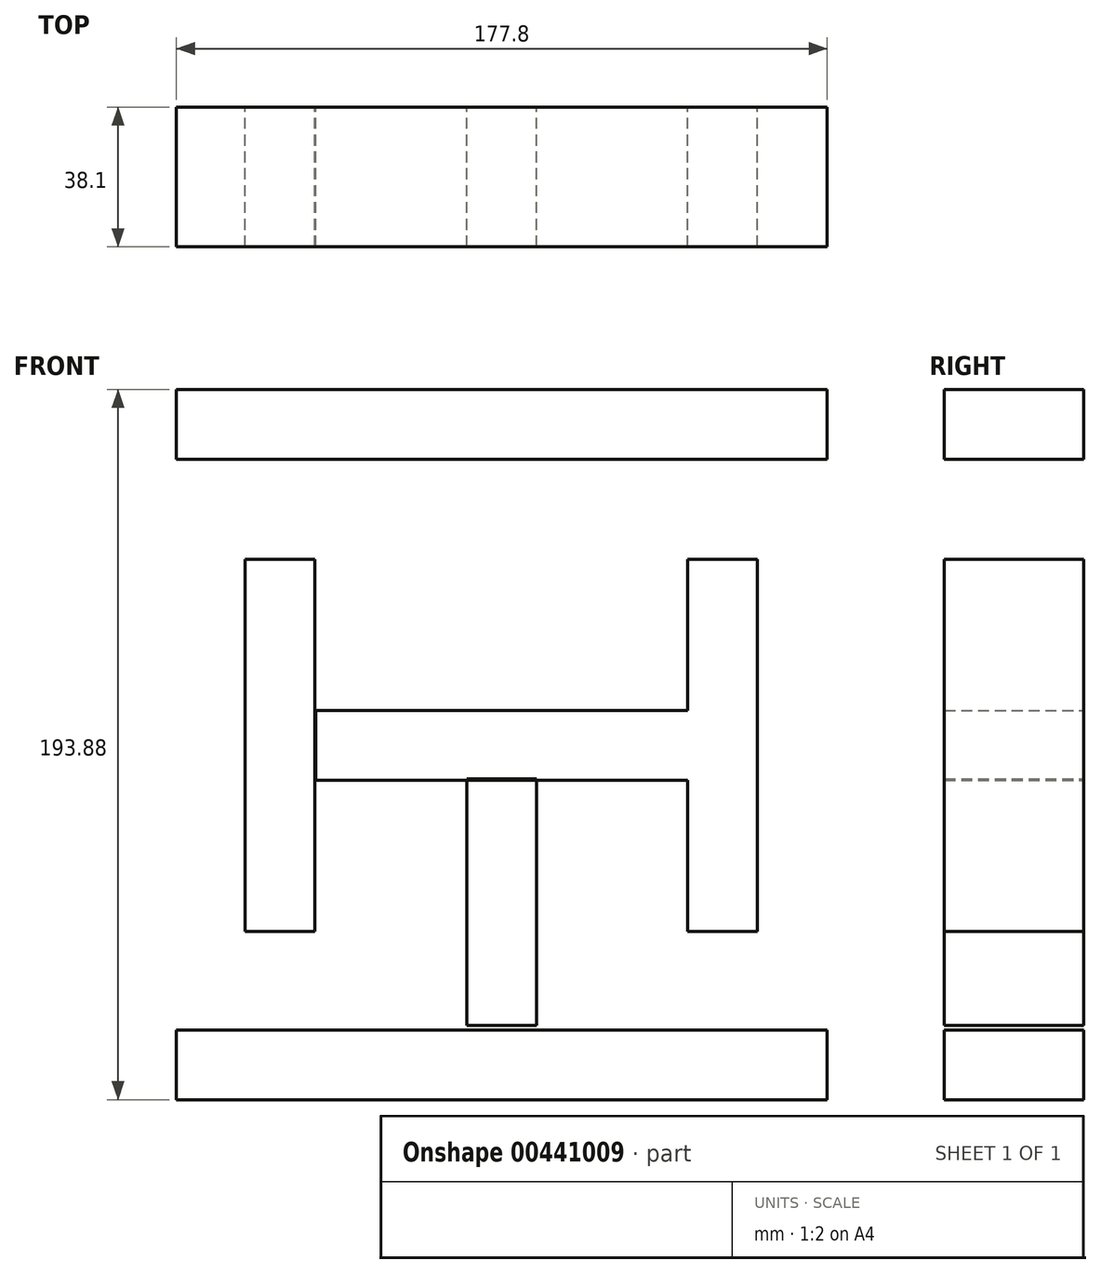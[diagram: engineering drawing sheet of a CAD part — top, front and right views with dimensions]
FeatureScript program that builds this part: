
annotation { "Feature Type Name" : "Feature", "Feature Type Description" : "" }
export const myFeature = defineFeature(function(context is Context, id is Id, definition is map)
    precondition{}
    {
        {
            var Q0;
            Q0=qCreatedBy(makeId("Front.planeOp"),FACE);
            var sketch = newSketch(context, id + "F0", { "sketchPlane" : qUnion([Q0])});
            skLineSegment(sketch, "E0.bottom", {"start": v(-88.9, 97.2) * mm, "end": v(88.9, 97.2) * mm});
            skLineSegment(sketch, "E0.top", {"start": v(-88.9, 78.15) * mm, "end": v(88.9, 78.15) * mm});
            skLineSegment(sketch, "E0.left", {"start": v(-88.9, 97.2) * mm, "end": v(-88.9, 78.15) * mm});
            skLineSegment(sketch, "E0.right", {"start": v(88.9, 97.2) * mm, "end": v(88.9, 78.15) * mm});
            skPoint(sketch, "E0.middle", {"position": v(0, 87.68) * mm});
            skLineSegment(sketch, "E1.bottom", {"start": v(-88.9, -96.68) * mm, "end": v(88.9, -96.68) * mm});
            skLineSegment(sketch, "E1.top", {"start": v(-88.9, -77.63) * mm, "end": v(88.9, -77.63) * mm});
            skLineSegment(sketch, "E1.left", {"start": v(-88.9, -96.68) * mm, "end": v(-88.9, -77.63) * mm});
            skLineSegment(sketch, "E1.right", {"start": v(88.9, -96.68) * mm, "end": v(88.9, -77.63) * mm});
            skPoint(sketch, "E1.middle", {"position": v(0, -87.16) * mm});
            skLineSegment(sketch, "E2.bottom", {"start": v(-9.53, 78.15) * mm, "end": v(9.52, 78.15) * mm});
            skLineSegment(sketch, "E2.top", {"start": v(-9.52, 10.84) * mm, "end": v(9.53, 10.84) * mm});
            skLineSegment(sketch, "E2.left", {"start": v(-9.53, 78.15) * mm, "end": v(-9.52, 10.84) * mm});
            skLineSegment(sketch, "E2.right", {"start": v(9.52, 78.15) * mm, "end": v(9.53, 10.84) * mm});
            skPoint(sketch, "E2.middle", {"position": v(0, 44.5) * mm});
            skLineSegment(sketch, "E3.bottom", {"start": v(-9.53, -9.12) * mm, "end": v(9.53, -9.12) * mm});
            skLineSegment(sketch, "E3.top", {"start": v(-9.53, -76.43) * mm, "end": v(9.52, -76.43) * mm});
            skLineSegment(sketch, "E3.left", {"start": v(-9.53, -9.12) * mm, "end": v(-9.53, -76.43) * mm});
            skLineSegment(sketch, "E3.right", {"start": v(9.53, -9.12) * mm, "end": v(9.52, -76.43) * mm});
            skPoint(sketch, "E3.middle", {"position": v(0, -42.78) * mm});
            skLineSegment(sketch, "E4.bottom", {"start": v(-50.8, 9.53) * mm, "end": v(50.8, 9.53) * mm});
            skLineSegment(sketch, "E4.top", {"start": v(-50.8, -9.52) * mm, "end": v(50.8, -9.52) * mm});
            skLineSegment(sketch, "E4.left", {"start": v(-50.8, 9.53) * mm, "end": v(-50.8, -9.52) * mm});
            skLineSegment(sketch, "E4.right", {"start": v(50.8, 9.53) * mm, "end": v(50.8, -9.52) * mm});
            skPoint(sketch, "E4.middle", {"position": v(0, 0) * mm});
            skLineSegment(sketch, "E5.bottom", {"start": v(50.8, 50.8) * mm, "end": v(69.85, 50.8) * mm});
            skLineSegment(sketch, "E5.top", {"start": v(50.8, -50.8) * mm, "end": v(69.85, -50.8) * mm});
            skLineSegment(sketch, "E5.left", {"start": v(50.8, 50.8) * mm, "end": v(50.8, -50.8) * mm});
            skLineSegment(sketch, "E5.right", {"start": v(69.85, 50.8) * mm, "end": v(69.85, -50.8) * mm});
            skPoint(sketch, "E5.middle", {"position": v(60.33, 0) * mm});
            skPoint(sketch, "E5.middle.positionSnap0", {"position": v(50.8, 0) * mm});
            skPoint(sketch, "E5.cornerSnap0", {"position": v(50.8, 0) * mm});
            skPoint(sketch, "E5.centerSnap0", {"position": v(50.8, 0) * mm});
            skLineSegment(sketch, "E6.bottom", {"start": v(-70.2, 50.8) * mm, "end": v(-51.15, 50.8) * mm});
            skLineSegment(sketch, "E6.top", {"start": v(-70.2, -50.8) * mm, "end": v(-51.15, -50.8) * mm});
            skLineSegment(sketch, "E6.left", {"start": v(-70.2, 50.8) * mm, "end": v(-70.2, -50.8) * mm});
            skLineSegment(sketch, "E6.right", {"start": v(-51.15, 50.8) * mm, "end": v(-51.15, -50.8) * mm});
            skPoint(sketch, "E6.middle", {"position": v(-60.67, 0) * mm});
            skPoint(sketch, "E6.middle.positionSnap0", {"position": v(-50.8, 0) * mm});
            skPoint(sketch, "E6.centerSnap0", {"position": v(-50.8, 0) * mm});
            skSolve(sketch);
        }
        {
            var Q0;
            Q0=makeQuery(id+"F0.imprint","IMPRINT",FACE,{"disambiguationData":[TD([[makeQuery(id+"F0.imprint","IMPRINT",EDGE,{"derivedFrom":sQuery(id+"F0.wireOp",EDGE,"E6.bottom")}),-1.0]])]});
            var Q1;
            {var subQ3=sQuery(id+"F0.wireOp",EDGE,"E5.bottom");Q1=makeQuery(id+"F0.imprint","IMPRINT",FACE,{"disambiguationData":[TD([[makeQuery(id+"F0.imprint","IMPRINT",EDGE,{"derivedFrom":subQ3}),-1.0]])]});}
            var Q2;
            {var subQ2=sQuery(id+"F0.wireOp",EDGE,"E3.bottom");Q2=makeQuery(id+"F0.imprint","IMPRINT",FACE,{"disambiguationData":[TD([[makeQuery(id+"F0.imprint","IMPRINT",EDGE,{"derivedFrom":subQ2}),1.0]])]});}
            var Q3;
            Q3=makeQuery(id+"F0.imprint","IMPRINT",FACE,{"disambiguationData":[TD([[makeQuery(id+"F0.imprint","IMPRINT",EDGE,{"derivedFrom":sQuery(id+"F0.wireOp",EDGE,"E2.bottom")}),-1.0]])]});
            var Q4;
            {var subQ0=sQuery(id+"F0.wireOp",EDGE,"E3.top");Q4=makeQuery(id+"F0.imprint","IMPRINT",FACE,{"disambiguationData":[TD([[makeQuery(id+"F0.imprint","IMPRINT",EDGE,{"derivedFrom":subQ0}),1.0]])]});}
            var Q5;
            Q5=makeQuery(id+"F0.imprint","IMPRINT",FACE,{"disambiguationData":[TD([[makeQuery(id+"F0.imprint","IMPRINT",EDGE,{"derivedFrom":sQuery(id+"F0.wireOp",EDGE,"E1.bottom")}),1.0]])]});
            var Q6;
            Q6=makeQuery(id+"F0.imprint","IMPRINT",FACE,{"disambiguationData":[TD([[makeQuery(id+"F0.imprint","IMPRINT",EDGE,{"derivedFrom":sQuery(id+"F0.wireOp",EDGE,"E0.bottom")}),-1.0]])]});
            extrude(context, id + "F1", {"entities" : qUnion([Q0, Q1, Q2, Q3, Q4, Q5, Q6]), "depth" : 38.1 * mm});
        }
    });
